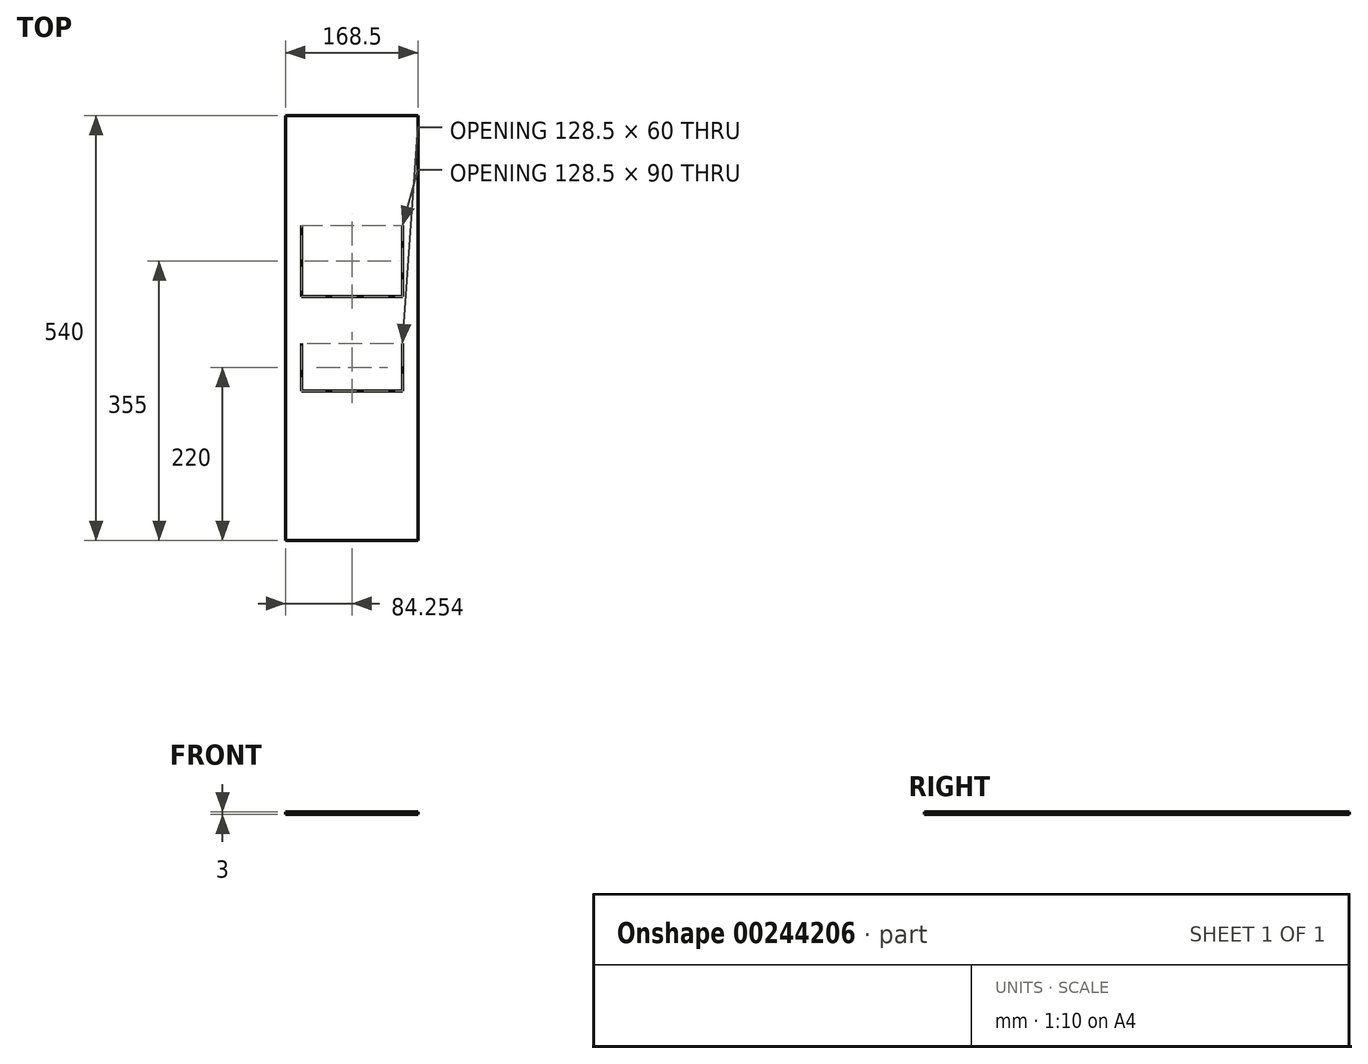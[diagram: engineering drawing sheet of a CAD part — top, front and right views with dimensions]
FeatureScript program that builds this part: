
annotation { "Feature Type Name" : "Feature", "Feature Type Description" : "" }
export const myFeature = defineFeature(function(context is Context, id is Id, definition is map)
    precondition{}
    {
        {
            var Q0;
            Q0=qCreatedBy(makeId("Top.planeOp"),FACE);
            var sketch = newSketch(context, id + "F0", { "sketchPlane" : qUnion([Q0])});
            skLineSegment(sketch, "E0.top", {"start": v(-67.95, -250) * mm, "end": v(100.55, -250) * mm});
            skLineSegment(sketch, "E0.left", {"start": v(-67.95, 250) * mm, "end": v(-67.95, -250) * mm});
            skLineSegment(sketch, "E0.right", {"start": v(100.55, 250) * mm, "end": v(100.55, -250) * mm});
            skLineSegment(sketch, "E1", {"start": v(-47.95, 150) * mm, "end": v(-47.95, 60) * mm});
            skLineSegment(sketch, "E2", {"start": v(-47.95, 60) * mm, "end": v(80.55, 60) * mm});
            skLineSegment(sketch, "E3", {"start": v(80.55, 60) * mm, "end": v(80.55, 150) * mm});
            skLineSegment(sketch, "E4", {"start": v(-47.95, 0) * mm, "end": v(-47.95, -60) * mm});
            skLineSegment(sketch, "E5", {"start": v(-47.95, -60) * mm, "end": v(80.55, -60) * mm});
            skLineSegment(sketch, "E6", {"start": v(80.55, -60) * mm, "end": v(80.55, 0) * mm});
            skLineSegment(sketch, "E7", {"start": v(-52.6, 20) * mm, "end": v(75.66, 20) * mm, "construction": true});
            skLineSegment(sketch, "E8", {"start": v(80.55, 0) * mm, "end": v(80.45, 0) * mm});
            skLineSegment(sketch, "E9", {"start": v(80.45, 0) * mm, "end": v(80.45, -60) * mm});
            skLineSegment(sketch, "E10", {"start": v(80.55, -59.9) * mm, "end": v(-47.95, -59.9) * mm});
            skLineSegment(sketch, "E11", {"start": v(-47.85, -60) * mm, "end": v(-47.85, 0) * mm});
            skLineSegment(sketch, "E12", {"start": v(-47.85, 0) * mm, "end": v(-47.95, 0) * mm});
            skLineSegment(sketch, "E13", {"start": v(80.45, 60) * mm, "end": v(80.45, 150) * mm});
            skLineSegment(sketch, "E14", {"start": v(80.45, 150) * mm, "end": v(80.55, 150) * mm});
            skLineSegment(sketch, "E15", {"start": v(-47.95, 60.1) * mm, "end": v(80.55, 60.1) * mm});
            skLineSegment(sketch, "E16", {"start": v(-47.85, 60) * mm, "end": v(-47.85, 150) * mm});
            skLineSegment(sketch, "E17", {"start": v(-47.85, 150) * mm, "end": v(-47.95, 150) * mm});
            skLineSegment(sketch, "E18", {"start": v(-67.95, 250) * mm, "end": v(-67.95, 290) * mm});
            skLineSegment(sketch, "E19", {"start": v(-67.95, 290) * mm, "end": v(100.55, 290) * mm});
            skLineSegment(sketch, "E20", {"start": v(100.55, 290) * mm, "end": v(100.55, 250) * mm});
            skSolve(sketch);
        }
        {
            var Q0;
            Q0 = qSketchRegion(id + "F0", true);
            extrude(context, id + "F1", {"entities" : qUnion([Q0]), "depth" : 3 * mm});
        }
    });
